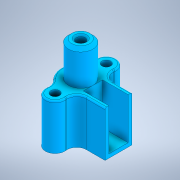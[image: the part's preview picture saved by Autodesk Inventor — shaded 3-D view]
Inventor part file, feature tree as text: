
AUTODESK INVENTOR PART (.ipt)
format: ipt  version: 2020 (Build 240168000, 168)  size: 232,448 bytes
history: native  units: mm
features: sketch x5, fillet x3, extrude x2, revolve x1, chamfer x1
ambient origin geometry x8: Origin, YZ Plane, XZ Plane, XY Plane, X Axis, Y Axis, Z Axis, Center Point
bodies: Solid1 (feature_tree)
feature tree (12):
  revolve  "Revolution1"  [1 undecoded]
  chamfer  "Chamfer1"  Distance=0.5mm Angle=45.0deg
  extrude  "Extrusion3"  Depth=8.0mm
  fillet  "Fillet1"  Radius=12.0mm
  sketch  "Sketch7"  dims[d20=3.8mm d21=0.5mm d22=2.0mm d23=45.0deg]
  sketch  "Sketch8"  dims[d24=6.0mm d26=8.0mm d27=12.0mm]
  extrude  "Extrusion4"  Depth=14.2mm TaperAngle=0.0deg
  fillet  "Fillet4"  Radius=4.0mm
  fillet  "Fillet5"  Radius=2.0mm
  sketch  "Sketch1"  dims[d1=1.4mm d8=1.0mm]
  sketch  "Sketch6"  dims[d9=90.0deg]
  sketch  "Sketch10"  dims[d28=2.7mm d29=14.2mm d30=0.0mm d31=4.0mm d33=2.0mm d34=8.4mm d35=11.8mm d39=6.0mm d40=1.2mm d41=13.0mm d42=8.0mm d43=0.0mm d44=3.0mm d45=0.5mm]
note: 1 required parameter value undecoded (feature->parameter linkage not recoverable at this tier; creation-order binding heuristic only, values carry confidence <= 0.55)
